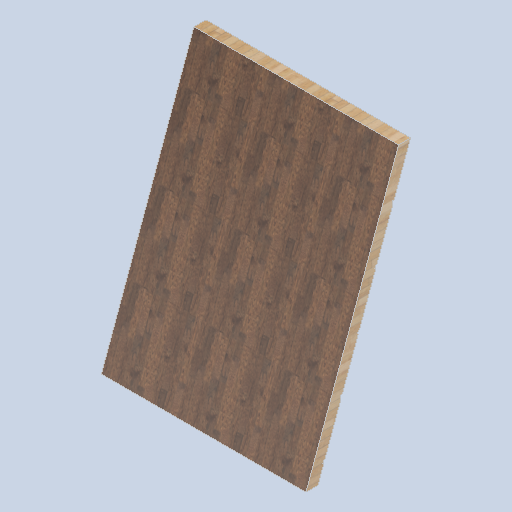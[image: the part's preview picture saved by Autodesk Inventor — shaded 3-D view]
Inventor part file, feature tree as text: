
AUTODESK INVENTOR PART (.ipt)
format: ipt  version: 2024.2 (Build 282272000, 272)  size: 294,912 bytes
history: native  units: in
note: dims shown in document units (in); Inventor stores cm internally (conversion verified against a paired STEP export)
features: other x3, sketch x2
ambient origin geometry x8: Origin, YZ Plane, XZ Plane, XY Plane, X Axis, Y Axis, Z Axis, Center Point
bodies: Solid1 (feature_tree)
feature tree (5):
  other  "side_curve_panel_02.ipt"
  other  "Solid1::side_curve_panel_02.ipt"
  other  "TaggingFeature1"
  sketch  "Sketch1"  dims[d0=0.3937in]
  sketch  "Sketch2"
